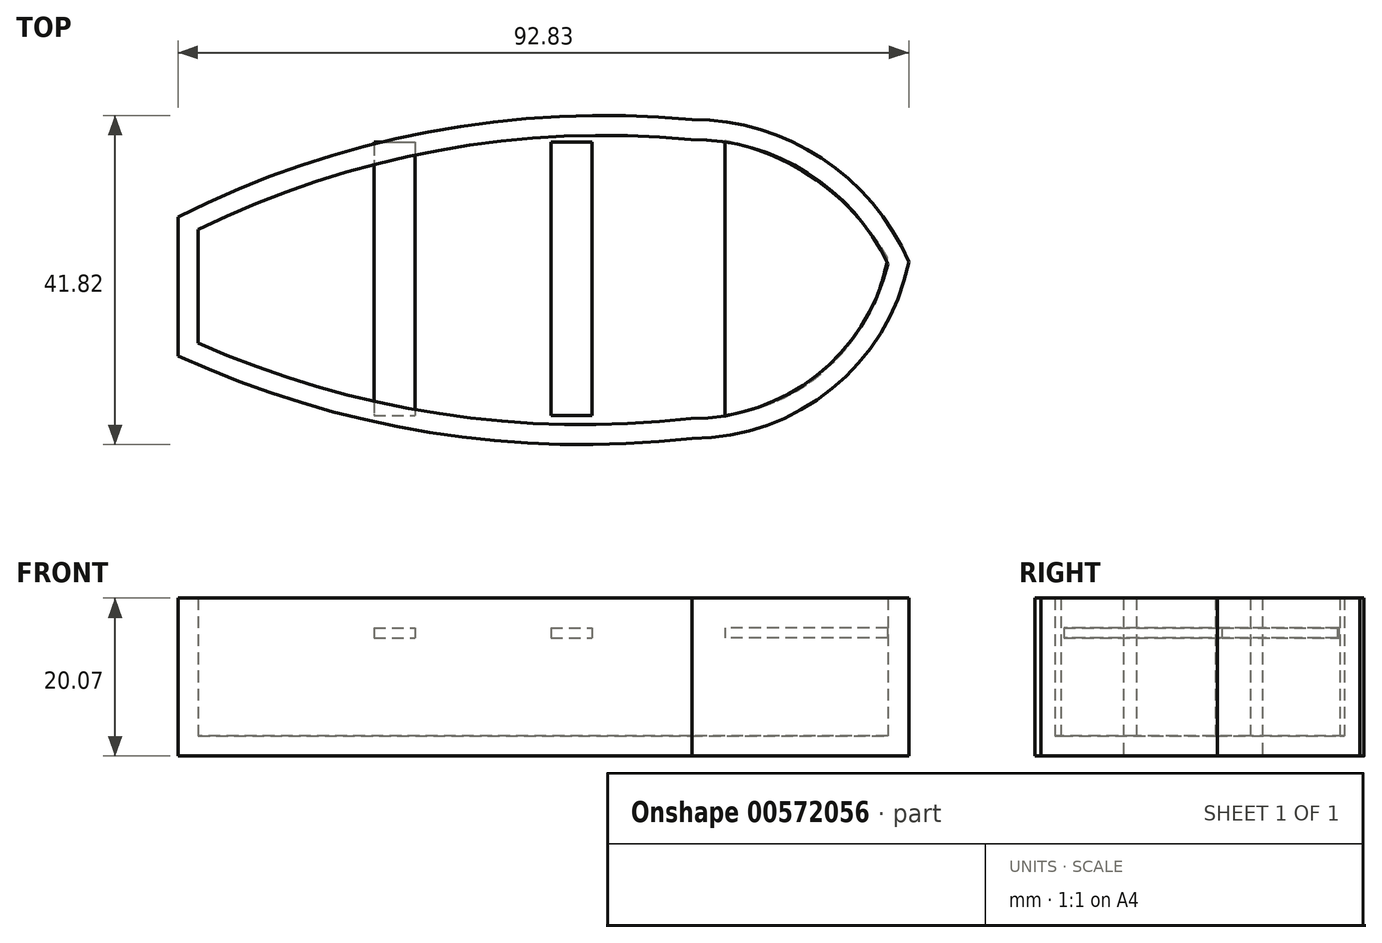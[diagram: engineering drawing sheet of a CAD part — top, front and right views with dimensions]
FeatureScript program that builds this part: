
annotation { "Feature Type Name" : "Feature", "Feature Type Description" : "" }
export const myFeature = defineFeature(function(context is Context, id is Id, definition is map)
    precondition{}
    {
        {
            var Q0;
            Q0=qCreatedBy(makeId("Top.planeOp"),FACE);
            var sketch = newSketch(context, id + "F0", { "sketchPlane" : qUnion([Q0])});
            skArc(sketch, "E0", {"start": v(42.33, 24.72) * mm, "mid": v(31.25, 37.88) * mm, "end": v(14.77, 42.81) * mm});
            skArc(sketch, "E1", {"start": v(14.77, 2.27) * mm, "mid": v(32.54, 8.6) * mm, "end": v(42.33, 24.72) * mm});
            skLineSegment(sketch, "E2", {"start": v(14.77, 42.81) * mm, "end": v(14.77, 2.27) * mm});
            skLineSegment(sketch, "E3", {"start": v(-50.5, 30.42) * mm, "end": v(-50.5, 12.77) * mm});
            skArc(sketch, "E4", {"start": v(14.77, 42.81) * mm, "mid": v(-18.74, 41.21) * mm, "end": v(-50.5, 30.42) * mm});
            skArc(sketch, "E5", {"start": v(-50.5, 12.77) * mm, "mid": v(-18.58, 3.06) * mm, "end": v(14.77, 2.27) * mm});
            skSolve(sketch);
        }
        {
            var Q0;
            Q0 = qSketchRegion(id + "F0", true);
            extrude(context, id + "F1", {"entities" : qUnion([Q0]), "depth" : 20.07 * mm, "offsetDistance" : 25.4 * mm});
        }
        {
            var Q0;
            Q0=makeQuery(id+"F1.opExtrude","CAP_FACE",FACE,{"disambiguationData":[OSD([sQuery(id+"F0.wireOp",EDGE,"HWol82R2-P8od-HedC-jz0Y-oSyAZcCyP6OR"),sQuery(id+"F0.wireOp",EDGE,"yGTrVZHS-N3MC-Fw7o-HvIH-kS2mrOcGAq8M"),sQuery(id+"F0.wireOp",EDGE,"GSCZsoGY-O1ra-Fvvf-Q5Zp-XjyPxAzI4hCJ"),sQuery(id+"F0.wireOp",EDGE,"E0"),sQuery(id+"F0.wireOp",EDGE,"E1")])],"isStart":false});
            shell(context, id + "F2", {"entities" : qUnion([Q0]), "thickness" : 2.54 * mm});
        }
        {
            var Q0;
            Q0=qCreatedBy(makeId("Top.planeOp"),FACE);
            cPlane(context, id + "F3", {"entities" : qUnion([Q0]), "cplaneType" : CPlaneType.OFFSET, "offset" : 15 * mm, "width" : 152.4 * mm, "height" : 152.4 * mm});
        }
        {
            var Q0;
            Q0=qCreatedBy(id+"F3.planeOp",FACE);
            var sketch = newSketch(context, id + "F4", { "sketchPlane" : qUnion([Q0])});
            skLineSegment(sketch, "E6.bottom", {"start": v(-3.16, 39.92) * mm, "end": v(2.07, 39.92) * mm});
            skLineSegment(sketch, "E6.top", {"start": v(-3.16, 5.17) * mm, "end": v(2.07, 5.17) * mm});
            skLineSegment(sketch, "E6.left", {"start": v(-3.16, 39.92) * mm, "end": v(-3.16, 5.17) * mm});
            skLineSegment(sketch, "E6.right", {"start": v(2.07, 39.92) * mm, "end": v(2.07, 5.17) * mm});
            skLineSegment(sketch, "E7.bottom", {"start": v(-25.64, 39.92) * mm, "end": v(-20.42, 39.92) * mm});
            skLineSegment(sketch, "E7.top", {"start": v(-25.64, 5.17) * mm, "end": v(-20.42, 5.17) * mm});
            skLineSegment(sketch, "E7.left", {"start": v(-25.64, 39.92) * mm, "end": v(-25.64, 5.17) * mm});
            skLineSegment(sketch, "E7.right", {"start": v(-20.42, 39.92) * mm, "end": v(-20.42, 5.17) * mm});
            skLineSegment(sketch, "E8", {"start": v(18.94, 40.1) * mm, "end": v(18.94, 5.17) * mm});
            skArc(sketch, "E9", {"start": v(39.62, 25.25) * mm, "mid": v(30.86, 34.88) * mm, "end": v(18.94, 40.1) * mm});
            skArc(sketch, "E10", {"start": v(18.94, 5.17) * mm, "mid": v(32.6, 11.8) * mm, "end": v(39.62, 25.25) * mm});
            skSolve(sketch);
        }
        {
            var Q0;
            Q0 = qSketchRegion(id + "F4", true);
            extrude(context, id + "F5", {"entities" : qUnion([Q0]), "depth" : 1.27 * mm, "offsetDistance" : 25.4 * mm});
        }
        {
            var Q0;
            Q0=qCreatedBy(makeId("Right.planeOp"),FACE);
            cPlane(context, id + "F6", {"entities" : qUnion([Q0]), "cplaneType" : CPlaneType.OFFSET, "offset" : 50.55 * mm, "oppositeDirection" : true, "width" : 152.4 * mm, "height" : 152.4 * mm});
        }
    });
